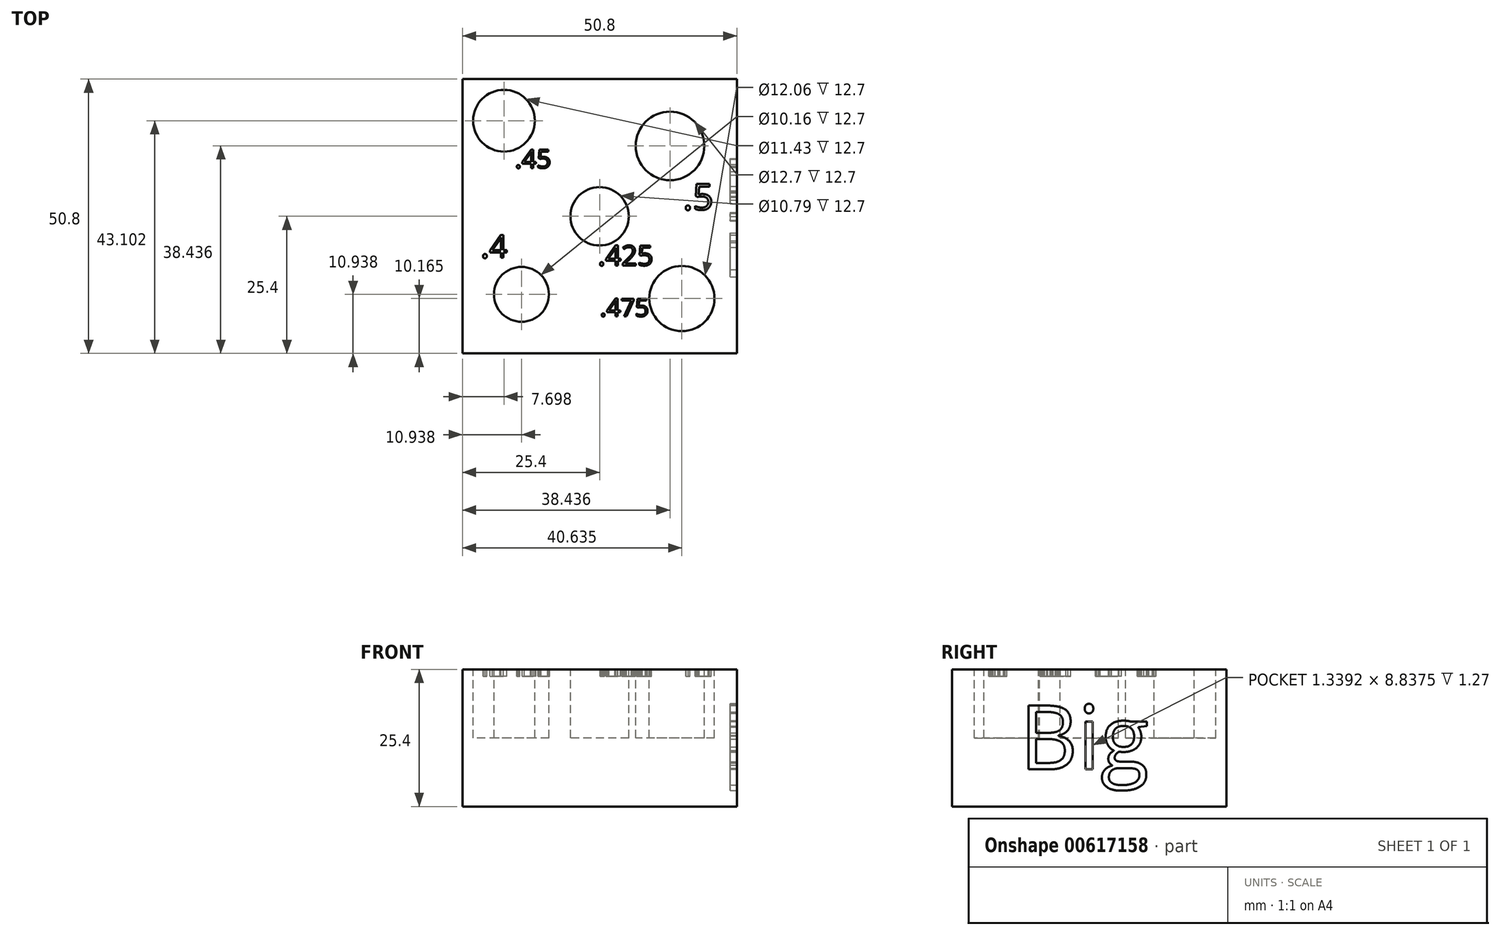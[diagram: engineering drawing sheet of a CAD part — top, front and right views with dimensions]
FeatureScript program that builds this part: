
annotation { "Feature Type Name" : "Feature", "Feature Type Description" : "" }
export const myFeature = defineFeature(function(context is Context, id is Id, definition is map)
    precondition{}
    {
        {
            var Q0;
            Q0=qCreatedBy(makeId("Top.planeOp"),FACE);
            var sketch = newSketch(context, id + "F0", { "sketchPlane" : qUnion([Q0])});
            skLineSegment(sketch, "E0.bottom", {"start": v(-25.4, 25.4) * mm, "end": v(25.4, 25.4) * mm});
            skLineSegment(sketch, "E0.top", {"start": v(-25.4, -25.4) * mm, "end": v(25.4, -25.4) * mm});
            skLineSegment(sketch, "E0.left", {"start": v(-25.4, 25.4) * mm, "end": v(-25.4, -25.4) * mm});
            skLineSegment(sketch, "E0.right", {"start": v(25.4, 25.4) * mm, "end": v(25.4, -25.4) * mm});
            skPoint(sketch, "E0.middle", {"position": v(0, 0) * mm});
            skSolve(sketch);
        }
        {
            var Q0;
            Q0 = qSketchRegion(id + "F0", true);
            extrude(context, id + "F1", {"entities" : qUnion([Q0]), "depth" : 25.4 * mm, "offsetDistance" : 25.4 * mm});
        }
        {
            var Q0;
            Q0=makeQuery(id+"F1.opExtrude","CAP_FACE",FACE,{"disambiguationData":[OSD([sQuery(id+"F0.wireOp",EDGE,"E0.bottom"),sQuery(id+"F0.wireOp",EDGE,"E0.top"),sQuery(id+"F0.wireOp",EDGE,"E0.left"),sQuery(id+"F0.wireOp",EDGE,"E0.right")])],"isStart":false});
            var sketch = newSketch(context, id + "F2", { "sketchPlane" : qUnion([Q0])});
            skCircle(sketch, "E1", {"center": v(0, 0) * mm, "radius": 5.4 * mm});
            skCircle(sketch, "E2", {"center": v(13.04, 13.04) * mm, "radius": 6.35 * mm});
            skCircle(sketch, "E3", {"center": v(-17.7, 17.7) * mm, "radius": 5.72 * mm});
            skCircle(sketch, "E4", {"center": v(-14.46, -14.46) * mm, "radius": 5.08 * mm});
            skCircle(sketch, "E5", {"center": v(15.23, -15.23) * mm, "radius": 6.03 * mm});
            skLineSegment(sketch, "E6", {"start": v(25.4, -25.4) * mm, "end": v(-25.4, 25.4) * mm, "construction": true});
            skLineSegment(sketch, "E7", {"start": v(-25.4, -25.4) * mm, "end": v(25.4, 25.4) * mm, "construction": true});
            skText(sketch, "E8", { "text": ".5", "fontName": "OpenSans-Regular.ttf"});
            skText(sketch, "E9", { "text": ".475\n", "fontName": "OpenSans-Regular.ttf"});
            skText(sketch, "E10", { "text": ".4", "fontName": "OpenSans-Regular.ttf"});
            skText(sketch, "E11", { "text": ".45", "fontName": "OpenSans-Regular.ttf"});
            const initialGuessF2  = {"E8": [0.01545, 0.00121, 1, 0, 0.00481], "E9": [6e-05, -0.01853, 1, 0, 0.0033], "E10": [-0.02202, -0.00769, 1, 0, 0.00426], "E11": [-0.01567, 0.00894, 1, 0, 0.00342]};
            skSetInitialGuess(sketch, initialGuessF2);
            skSolve(sketch);
        }
        {
            var Q0;
            Q0=makeQuery(id+"F2.imprint","IMPRINT",FACE,{"disambiguationData":[TD([[makeQuery(id+"F2.imprint","IMPRINT",EDGE,{"derivedFrom":sQuery(id+"F2.wireOp",EDGE,"E5")}),1.0]])]});
            var Q1;
            Q1=makeQuery(id+"F2.imprint","IMPRINT",FACE,{"disambiguationData":[TD([[makeQuery(id+"F2.imprint","IMPRINT",EDGE,{"derivedFrom":sQuery(id+"F2.wireOp",EDGE,"E4")}),1.0]])]});
            var Q2;
            Q2=makeQuery(id+"F2.imprint","IMPRINT",FACE,{"disambiguationData":[TD([[makeQuery(id+"F2.imprint","IMPRINT",EDGE,{"derivedFrom":sQuery(id+"F2.wireOp",EDGE,"E3")}),1.0]])]});
            var Q3;
            Q3=makeQuery(id+"F2.imprint","IMPRINT",FACE,{"disambiguationData":[TD([[makeQuery(id+"F2.imprint","IMPRINT",EDGE,{"derivedFrom":sQuery(id+"F2.wireOp",EDGE,"E2")}),1.0]])]});
            var Q4;
            Q4=makeQuery(id+"F2.imprint","IMPRINT",FACE,{"disambiguationData":[TD([[makeQuery(id+"F2.imprint","IMPRINT",EDGE,{"derivedFrom":sQuery(id+"F2.wireOp",EDGE,"E1")}),1.0]])]});
            extrude(context, id + "F3", {"entities" : qUnion([Q0, Q1, Q2, Q3, Q4]), "operationType" : NewBodyOperationType.REMOVE, "oppositeDirection" : true, "depth" : 12.7 * mm, "offsetDistance" : 25.4 * mm});
        }
        {
            var Q0;
            Q0=makeQuery(id+"F2.imprint","IMPRINT",FACE,{"disambiguationData":[TD([[makeQuery(id+"F2.imprint","IMPRINT",EDGE,{"derivedFrom":sQuery(id+"F2.wireOp",EDGE,"E8.sketch_text.stroke-0")}),-1.0]])]});
            var Q1;
            Q1=makeQuery(id+"F2.imprint","IMPRINT",FACE,{"disambiguationData":[TD([[makeQuery(id+"F2.imprint","IMPRINT",EDGE,{"derivedFrom":sQuery(id+"F2.wireOp",EDGE,"E8.sketch_text.stroke-8")}),-1.0]])]});
            var Q2;
            Q2=makeQuery(id+"F2.imprint","IMPRINT",FACE,{"disambiguationData":[TD([[makeQuery(id+"F2.imprint","IMPRINT",EDGE,{"derivedFrom":sQuery(id+"F2.wireOp",EDGE,"E9.sketch_text.stroke-0")}),-1.0]])]});
            var Q3;
            Q3=makeQuery(id+"F2.imprint","IMPRINT",FACE,{"disambiguationData":[TD([[makeQuery(id+"F2.imprint","IMPRINT",EDGE,{"derivedFrom":sQuery(id+"F2.wireOp",EDGE,"E9.sketch_text.stroke-25")}),-1.0]])]});
            var Q4;
            Q4=makeQuery(id+"F2.imprint","IMPRINT",FACE,{"disambiguationData":[TD([[makeQuery(id+"F2.imprint","IMPRINT",EDGE,{"derivedFrom":sQuery(id+"F2.wireOp",EDGE,"E9.sketch_text.stroke-32")}),-1.0]])]});
            var Q5;
            Q5=makeQuery(id+"F2.imprint","IMPRINT",FACE,{"disambiguationData":[TD([[makeQuery(id+"F2.imprint","IMPRINT",EDGE,{"derivedFrom":sQuery(id+"F2.wireOp",EDGE,"E10.sketch_text.stroke-0")}),-1.0]])]});
            var Q6;
            Q6=makeQuery(id+"F2.imprint","IMPRINT",FACE,{"disambiguationData":[TD([[makeQuery(id+"F2.imprint","IMPRINT",EDGE,{"derivedFrom":sQuery(id+"F2.wireOp",EDGE,"E11.sketch_text.stroke-0")}),-1.0]])]});
            var Q7;
            Q7=makeQuery(id+"F2.imprint","IMPRINT",FACE,{"disambiguationData":[TD([[makeQuery(id+"F2.imprint","IMPRINT",EDGE,{"derivedFrom":sQuery(id+"F2.wireOp",EDGE,"E11.sketch_text.stroke-25")}),-1.0]])]});
            var Q8;
            Q8=makeQuery(id+"F2.imprint","IMPRINT",FACE,{"disambiguationData":[TD([[makeQuery(id+"F2.imprint","IMPRINT",EDGE,{"derivedFrom":sQuery(id+"F2.wireOp",EDGE,"E9.sketch_text.stroke-8")}),-1.0]])]});
            var Q9;
            Q9=makeQuery(id+"F2.imprint","IMPRINT",FACE,{"disambiguationData":[TD([[makeQuery(id+"F2.imprint","IMPRINT",EDGE,{"derivedFrom":sQuery(id+"F2.wireOp",EDGE,"E10.sketch_text.stroke-8")}),-1.0]])]});
            var Q10;
            Q10=makeQuery(id+"F2.imprint","IMPRINT",FACE,{"disambiguationData":[TD([[makeQuery(id+"F2.imprint","IMPRINT",EDGE,{"derivedFrom":sQuery(id+"F2.wireOp",EDGE,"E11.sketch_text.stroke-8")}),-1.0]])]});
            extrude(context, id + "F4", {"entities" : qUnion([Q0, Q1, Q2, Q3, Q4, Q5, Q6, Q7, Q8, Q9, Q10]), "operationType" : NewBodyOperationType.REMOVE, "oppositeDirection" : true, "depth" : 1.27 * mm, "offsetDistance" : 25.4 * mm});
        }
        {
            var Q0;
            {var subQ0=sQuery(id+"F0.wireOp",EDGE,"E0.left");var subQ1=sQuery(id+"F0.wireOp",EDGE,"E0.top");var subQ2=sQuery(id+"F0.wireOp",EDGE,"E0.right");var subQ3=sQuery(id+"F0.wireOp",EDGE,"E0.bottom");Q0=makeQuery(id+"F4.boolean.opBoolean","SPLIT",FACE,{"disambiguationData":[TD([makeQuery(id+"F1.opExtrude","SWEPT_FACE",FACE,{"disambiguationData":[OSD([subQ3])]})])],"derivedFrom":makeQuery(id+"F1.opExtrude","CAP_FACE",FACE,{"disambiguationData":[OSD([subQ3,subQ1,subQ0,subQ2])],"isStart":false})});}
            var sketch = newSketch(context, id + "F5", { "sketchPlane" : qUnion([Q0])});
            skText(sketch, "E12", { "text": ".425", "fontName": "OpenSans-Regular.ttf"});
            const initialGuessF5  = {"E12": [-0.0003, -0.00911, 1, 0, 0.00372]};
            skSetInitialGuess(sketch, initialGuessF5);
            skSolve(sketch);
        }
        {
            var Q0;
            Q0 = qSketchRegion(id + "F5", true);
            extrude(context, id + "F6", {"entities" : qUnion([Q0]), "operationType" : NewBodyOperationType.REMOVE, "oppositeDirection" : true, "depth" : 1.27 * mm, "offsetDistance" : 25.4 * mm});
        }
        {
            var Q0;
            Q0=makeQuery(id+"F1.opExtrude","SWEPT_FACE",FACE,{"disambiguationData":[OSD([sQuery(id+"F0.wireOp",EDGE,"E0.right")])]});
            var sketch = newSketch(context, id + "F7", { "sketchPlane" : qUnion([Q0])});
            skText(sketch, "E13", { "text": "Big", "fontName": "OpenSans-Regular.ttf"});
            const initialGuessF7  = {"E13": [-0.01286, 0.0069, 1, 0, 0.01189]};
            skSetInitialGuess(sketch, initialGuessF7);
            skSolve(sketch);
        }
        {
            var Q0;
            Q0 = qSketchRegion(id + "F7", true);
            extrude(context, id + "F8", {"entities" : qUnion([Q0]), "operationType" : NewBodyOperationType.REMOVE, "oppositeDirection" : true, "depth" : 1.27 * mm, "offsetDistance" : 25.4 * mm});
        }
    });
